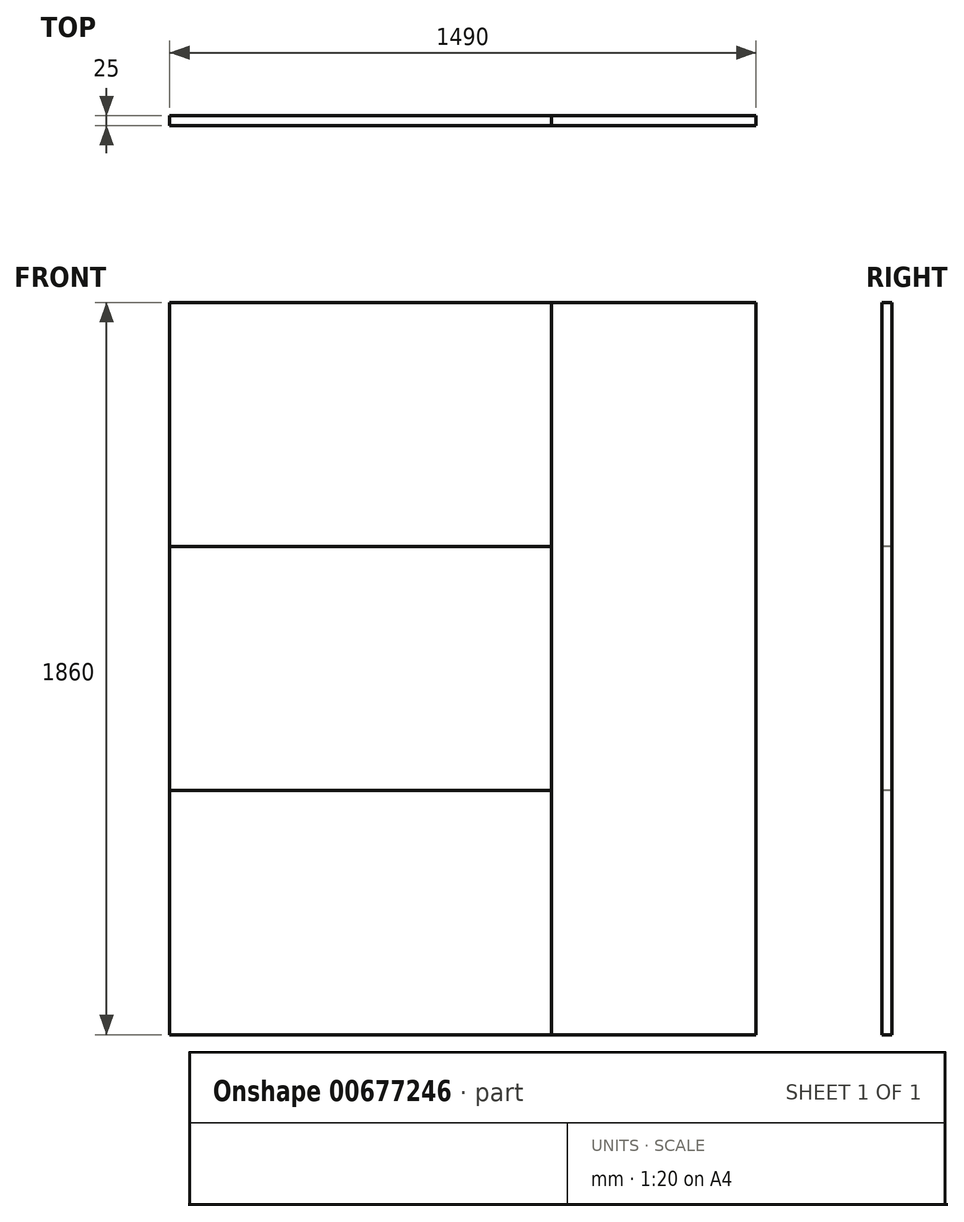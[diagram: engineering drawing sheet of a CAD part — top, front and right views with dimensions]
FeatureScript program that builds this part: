
annotation { "Feature Type Name" : "Feature", "Feature Type Description" : "" }
export const myFeature = defineFeature(function(context is Context, id is Id, definition is map)
    precondition{}
    {
        {
            var Q0;
            Q0=qCreatedBy(makeId("Front.planeOp"),FACE);
            var sketch = newSketch(context, id + "F0", { "sketchPlane" : qUnion([Q0])});
            skLineSegment(sketch, "E0.bottom", {"start": v(-857.14, 930) * mm, "end": v(632.86, 930) * mm});
            skLineSegment(sketch, "E0.top", {"start": v(-857.14, -930) * mm, "end": v(632.86, -930) * mm});
            skLineSegment(sketch, "E0.left", {"start": v(-857.14, 930) * mm, "end": v(-857.14, -930) * mm});
            skLineSegment(sketch, "E0.right", {"start": v(632.86, 930) * mm, "end": v(632.86, -930) * mm});
            skLineSegment(sketch, "E1", {"start": v(112.86, 930) * mm, "end": v(112.86, -930) * mm});
            skLineSegment(sketch, "E2", {"start": v(-857.14, 310) * mm, "end": v(112.86, 310) * mm});
            skLineSegment(sketch, "E3", {"start": v(-857.14, -310) * mm, "end": v(112.86, -310) * mm});
            skSolve(sketch);
        }
        {
            var Q0;
            Q0=sQuery(id+"F0.wireOp",EDGE,"E0.right");
            extrude(context, id + "F1", {"bodyType" : ToolBodyType.SURFACE, "surfaceEntities" : qUnion([Q0]), "depth" : 25 * mm, "offsetDistance" : 25 * mm});
        }
        {
            var Q0;
            Q0=sQuery(id+"F0.wireOp",EDGE,"E2");
            var Q1;
            Q1=sQuery(id+"F0.wireOp",EDGE,"E0.bottom");
            extrude(context, id + "F2", {"bodyType" : ToolBodyType.SURFACE, "surfaceEntities" : qUnion([Q0, Q1]), "depth" : 25 * mm, "offsetDistance" : 25 * mm});
        }
        {
            var Q0;
            Q0=sQuery(id+"F0.wireOp",EDGE,"E0.left");
            var Q1;
            Q1=sQuery(id+"F0.wireOp",EDGE,"E1");
            extrude(context, id + "F3", {"bodyType" : ToolBodyType.SURFACE, "surfaceEntities" : qUnion([Q0, Q1]), "depth" : 25 * mm, "offsetDistance" : 25 * mm});
        }
        {
            var Q0;
            Q0=sQuery(id+"F0.wireOp",EDGE,"E3");
            var Q1;
            Q1=sQuery(id+"F0.wireOp",EDGE,"E0.top");
            extrude(context, id + "F4", {"bodyType" : ToolBodyType.SURFACE, "surfaceEntities" : qUnion([Q0, Q1]), "depth" : 25 * mm, "offsetDistance" : 25 * mm});
        }
    });
